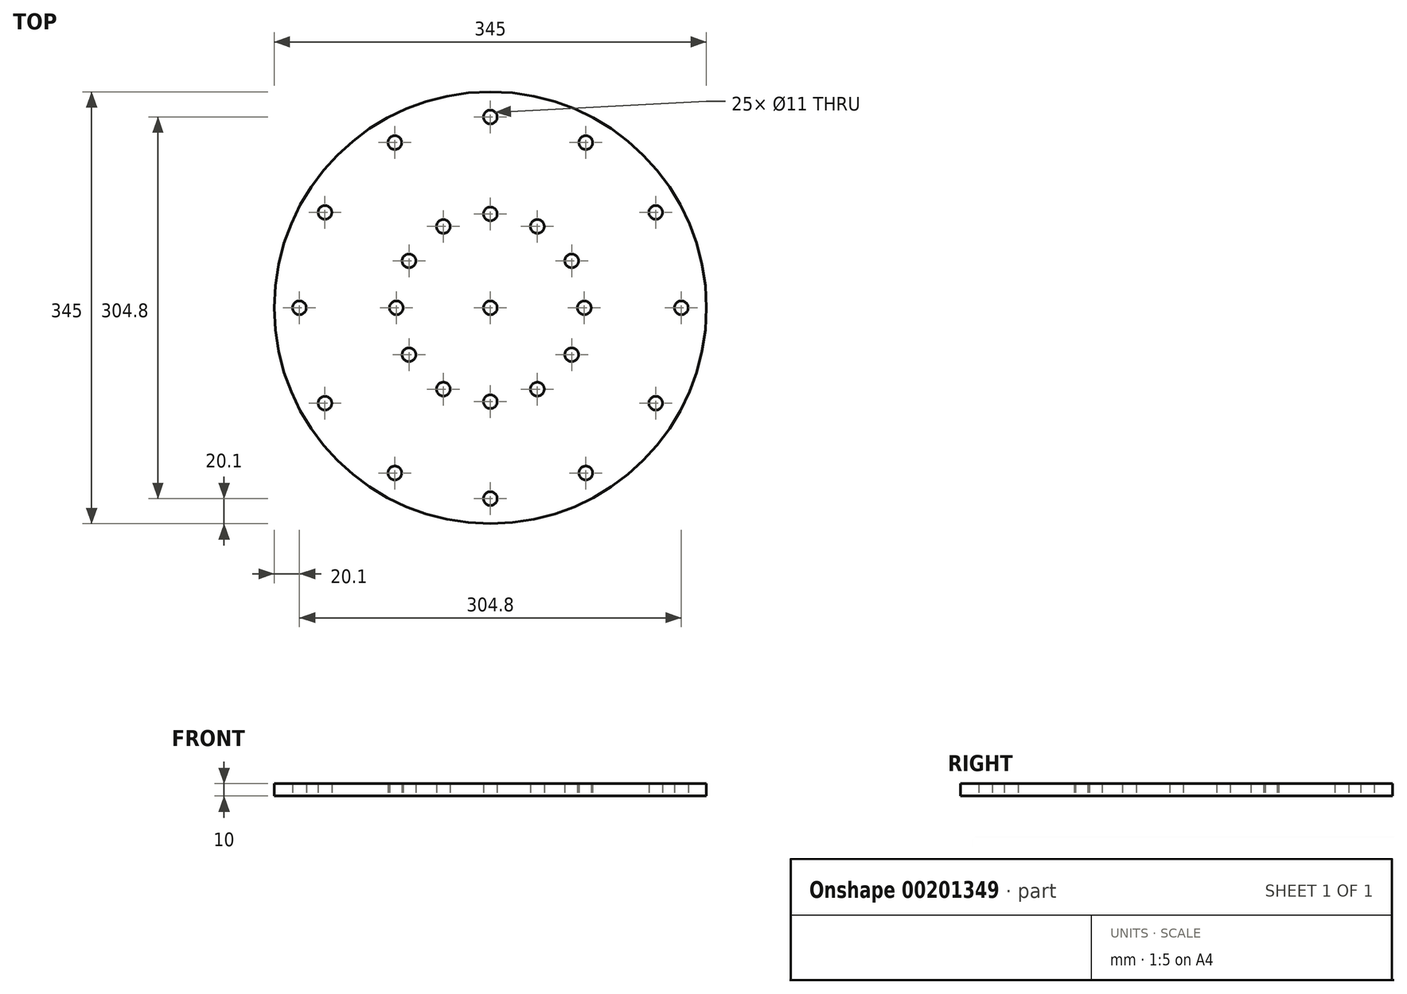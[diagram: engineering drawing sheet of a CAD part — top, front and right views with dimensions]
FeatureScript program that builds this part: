
annotation { "Feature Type Name" : "Feature", "Feature Type Description" : "" }
export const myFeature = defineFeature(function(context is Context, id is Id, definition is map)
    precondition{}
    {
        {
            var Q0;
            Q0=qCreatedBy(makeId("Top.planeOp"),FACE);
            var sketch = newSketch(context, id + "F0", { "sketchPlane" : qUnion([Q0])});
            skCircle(sketch, "E0", {"center": v(0, 0) * mm, "radius": 172.5 * mm});
            skLineSegment(sketch, "E1", {"start": v(0, 172.5) * mm, "end": v(0, -172.5) * mm, "construction": true});
            skCircle(sketch, "E2", {"center": v(0, 0) * mm, "radius": 152.4 * mm, "construction": true});
            skCircle(sketch, "E3", {"center": v(0, 0) * mm, "radius": 75 * mm, "construction": true});
            skLineSegment(sketch, "E4", {"start": v(172.5, 0) * mm, "end": v(-172.5, 0) * mm, "construction": true});
            skPoint(sketch, "E5", {"position": v(0, 152.4) * mm});
            skCircle(sketch, "E6", {"center": v(0, 152.4) * mm, "radius": 5.5 * mm});
            skCircle(sketch, "E7.1.0", {"center": v(-76.2, 131.98) * mm, "radius": 5.5 * mm});
            skCircle(sketch, "E7.2.0", {"center": v(-131.98, 76.2) * mm, "radius": 5.5 * mm});
            skCircle(sketch, "E7.3.0", {"center": v(-152.4, 0) * mm, "radius": 5.5 * mm});
            skCircle(sketch, "E7.4.0", {"center": v(-131.98, -76.2) * mm, "radius": 5.5 * mm});
            skCircle(sketch, "E7.5.0", {"center": v(-76.2, -131.98) * mm, "radius": 5.5 * mm});
            skCircle(sketch, "E7.6.0", {"center": v(0, -152.4) * mm, "radius": 5.5 * mm});
            skCircle(sketch, "E7.7.0", {"center": v(76.2, -131.98) * mm, "radius": 5.5 * mm});
            skCircle(sketch, "E7.8.0", {"center": v(131.98, -76.2) * mm, "radius": 5.5 * mm});
            skCircle(sketch, "E7.9.0", {"center": v(152.4, 0) * mm, "radius": 5.5 * mm});
            skCircle(sketch, "E7.10.0", {"center": v(131.98, 76.2) * mm, "radius": 5.5 * mm});
            skCircle(sketch, "E7.11.0", {"center": v(76.2, 131.98) * mm, "radius": 5.5 * mm});
            skLineSegment(sketch, "E7.anchor1", {"start": v(0, 0) * mm, "end": v(0, 152.4) * mm, "construction": true});
            skLineSegment(sketch, "E7.anchor2", {"start": v(0, 0) * mm, "end": v(76.2, 131.98) * mm, "construction": true});
            skPoint(sketch, "E8", {"position": v(0, 75) * mm});
            skCircle(sketch, "E9", {"center": v(0, 75) * mm, "radius": 5.5 * mm});
            skCircle(sketch, "E10.1.0", {"center": v(37.5, 64.95) * mm, "radius": 5.5 * mm});
            skCircle(sketch, "E10.2.0", {"center": v(64.95, 37.5) * mm, "radius": 5.5 * mm});
            skCircle(sketch, "E10.3.0", {"center": v(75, 0) * mm, "radius": 5.5 * mm});
            skCircle(sketch, "E10.4.0", {"center": v(64.95, -37.5) * mm, "radius": 5.5 * mm});
            skCircle(sketch, "E10.5.0", {"center": v(37.5, -64.95) * mm, "radius": 5.5 * mm});
            skCircle(sketch, "E10.6.0", {"center": v(0, -75) * mm, "radius": 5.5 * mm});
            skCircle(sketch, "E10.7.0", {"center": v(-37.5, -64.95) * mm, "radius": 5.5 * mm});
            skCircle(sketch, "E10.8.0", {"center": v(-64.95, -37.5) * mm, "radius": 5.5 * mm});
            skCircle(sketch, "E10.9.0", {"center": v(-75, 0) * mm, "radius": 5.5 * mm});
            skCircle(sketch, "E10.10.0", {"center": v(-64.95, 37.5) * mm, "radius": 5.5 * mm});
            skCircle(sketch, "E10.11.0", {"center": v(-37.5, 64.95) * mm, "radius": 5.5 * mm});
            skLineSegment(sketch, "E10.anchor1", {"start": v(0, 0) * mm, "end": v(0, 75) * mm, "construction": true});
            skLineSegment(sketch, "E10.anchor2", {"start": v(0, 0) * mm, "end": v(-37.5, 64.95) * mm, "construction": true});
            skCircle(sketch, "E11", {"center": v(0, 0) * mm, "radius": 5.5 * mm});
            skSolve(sketch);
        }
        {
            var Q0;
            Q0=makeQuery(id+"F0.imprint","IMPRINT",FACE,{"disambiguationData":[TD([[makeQuery(id+"F0.imprint","IMPRINT",EDGE,{"derivedFrom":sQuery(id+"F0.wireOp",EDGE,"E6")}),-1.0]])]});
            extrude(context, id + "F1", {"entities" : qUnion([Q0]), "depth" : 10 * mm});
        }
    });
